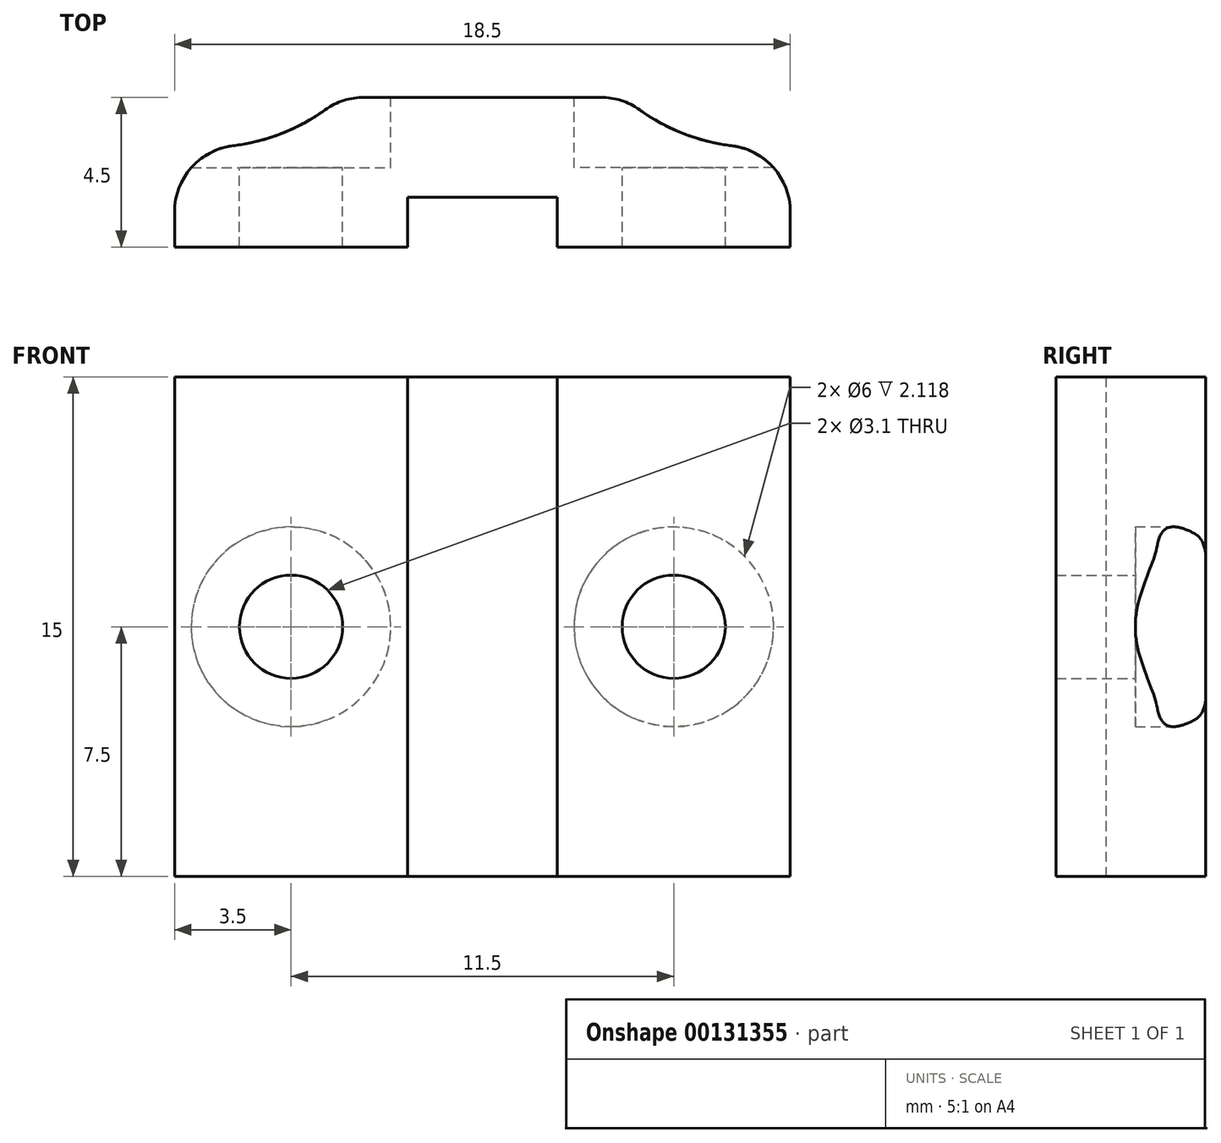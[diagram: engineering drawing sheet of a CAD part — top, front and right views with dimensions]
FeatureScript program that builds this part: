
annotation { "Feature Type Name" : "Feature", "Feature Type Description" : "" }
export const myFeature = defineFeature(function(context is Context, id is Id, definition is map)
    precondition{}
    {
        {
            var Q0;
            Q0=qCreatedBy(makeId("Top.planeOp"),FACE);
            var sketch = newSketch(context, id + "F0", { "sketchPlane" : qUnion([Q0])});
            skLineSegment(sketch, "E0", {"start": v(0, 0) * mm, "end": v(0, 3) * mm});
            skLineSegment(sketch, "E1", {"start": v(0, 3) * mm, "end": v(5, 3) * mm});
            skLineSegment(sketch, "E2", {"start": v(5, 3) * mm, "end": v(5, 4.5) * mm});
            skLineSegment(sketch, "E3", {"start": v(5, 4.5) * mm, "end": v(13.5, 4.5) * mm});
            skLineSegment(sketch, "E4", {"start": v(13.5, 4.5) * mm, "end": v(13.5, 3) * mm});
            skLineSegment(sketch, "E5", {"start": v(13.5, 3) * mm, "end": v(18.5, 3) * mm});
            skLineSegment(sketch, "E6", {"start": v(18.5, 3) * mm, "end": v(18.5, 0) * mm});
            skLineSegment(sketch, "E7", {"start": v(18.5, 0) * mm, "end": v(11.5, 0) * mm});
            skLineSegment(sketch, "E8", {"start": v(11.5, 0) * mm, "end": v(11.5, 1.5) * mm});
            skLineSegment(sketch, "E9", {"start": v(11.5, 1.5) * mm, "end": v(7, 1.5) * mm});
            skLineSegment(sketch, "E10", {"start": v(7, 1.5) * mm, "end": v(7, 0) * mm});
            skLineSegment(sketch, "E11", {"start": v(7, 0) * mm, "end": v(0, 0) * mm});
            skSolve(sketch);
        }
        {
            var Q0;
            Q0=qSketchRegion(id+"F0",true);
            extrude(context, id + "F1", {"entities" : qUnion([Q0]), "depth" : 15 * mm});
        }
        {
            var Q0;
            Q0=makeQuery(id+"F1.opExtrude","SWEPT_FACE",FACE,{"disambiguationData":[OSD([sQuery(id+"F0.wireOp",EDGE,"E3")])]});
            cPlane(context, id + "F2", {"entities" : qUnion([Q0]), "cplaneType" : CPlaneType.OFFSET, "offset" : 0 * mm, "width" : 150 * mm, "height" : 150 * mm});
        }
        {
            var Q0;
            Q0=makeQuery(id+"F1.opExtrude","SWEPT_EDGE",EDGE,{"disambiguationData":[OSD([sQuery(id+"F0.wireOp",EDGE,"E4"),sQuery(id+"F0.wireOp",EDGE,"E5")])]});
            var Q1;
            Q1=makeQuery(id+"F1.opExtrude","SWEPT_EDGE",EDGE,{"disambiguationData":[OSD([sQuery(id+"F0.wireOp",EDGE,"E1"),sQuery(id+"F0.wireOp",EDGE,"E2")])]});
            fillet(context, id + "F3", {"entities" : qUnion([Q0, Q1]), "radius" : 6 * mm, "tangentPropagation" : true, "allowEdgeOverflow" : false});
        }
        {
            var Q0;
            Q0=makeQuery(id+"F3.opFillet","BLEND_EDGE",EDGE,{"blendedFrom":[makeQuery(id+"F1.opExtrude","SWEPT_EDGE",EDGE,{"disambiguationData":[OSD([sQuery(id+"F0.wireOp",EDGE,"E4"),sQuery(id+"F0.wireOp",EDGE,"E5")])]}),makeQuery(id+"F1.opExtrude","SWEPT_FACE",FACE,{"disambiguationData":[OSD([sQuery(id+"F0.wireOp",EDGE,"E3")])]})],"blendedInto":[makeQuery(id+"F1.opExtrude","SWEPT_FACE",FACE,{"disambiguationData":[OSD([sQuery(id+"F0.wireOp",EDGE,"E3")])]})]});
            var Q1;
            Q1=makeQuery(id+"F3.opFillet","BLEND_EDGE",EDGE,{"blendedFrom":[makeQuery(id+"F1.opExtrude","SWEPT_EDGE",EDGE,{"disambiguationData":[OSD([sQuery(id+"F0.wireOp",EDGE,"E1"),sQuery(id+"F0.wireOp",EDGE,"E2")])]}),makeQuery(id+"F1.opExtrude","SWEPT_FACE",FACE,{"disambiguationData":[OSD([sQuery(id+"F0.wireOp",EDGE,"E3")])]})],"blendedInto":[makeQuery(id+"F1.opExtrude","SWEPT_FACE",FACE,{"disambiguationData":[OSD([sQuery(id+"F0.wireOp",EDGE,"E3")])]})]});
            var Q2;
            Q2=makeQuery(id+"F1.opExtrude","SWEPT_EDGE",EDGE,{"disambiguationData":[OSD([sQuery(id+"F0.wireOp",EDGE,"E5"),sQuery(id+"F0.wireOp",EDGE,"E6")])]});
            var Q3;
            Q3=makeQuery(id+"F1.opExtrude","SWEPT_EDGE",EDGE,{"disambiguationData":[OSD([sQuery(id+"F0.wireOp",EDGE,"E0"),sQuery(id+"F0.wireOp",EDGE,"E1")])]});
            fillet(context, id + "F4", {"entities" : qUnion([Q0, Q1, Q2, Q3]), "radius" : 2 * mm, "tangentPropagation" : true, "allowEdgeOverflow" : false});
        }
        {
            var Q0;
            Q0=qCreatedBy(id+"F2.planeOp",FACE);
            var sketch = newSketch(context, id + "F5", { "sketchPlane" : qUnion([Q0])});
            skPoint(sketch, "E12", {"position": v(-15, 7.5) * mm});
            skPoint(sketch, "E13", {"position": v(-3.5, 7.5) * mm});
            skSolve(sketch);
        }
        {
            var Q0;
            Q0=sQuery(id+"F5.wireOp",VERTEX,"E12");
            var Q1;
            Q1=sQuery(id+"F5.wireOp",VERTEX,"E13");
            var Q2;
            Q2=makeQuery(id+"F1.opExtrude","SWEPT_BODY",BODY,{"disambiguationData":[OSD([sQuery(id+"F0.wireOp",EDGE,"E0"),sQuery(id+"F0.wireOp",EDGE,"E1"),sQuery(id+"F0.wireOp",EDGE,"E2"),sQuery(id+"F0.wireOp",EDGE,"E3"),sQuery(id+"F0.wireOp",EDGE,"E4"),sQuery(id+"F0.wireOp",EDGE,"E5"),sQuery(id+"F0.wireOp",EDGE,"E6"),sQuery(id+"F0.wireOp",EDGE,"E7"),sQuery(id+"F0.wireOp",EDGE,"E8"),sQuery(id+"F0.wireOp",EDGE,"E9"),sQuery(id+"F0.wireOp",EDGE,"E10"),sQuery(id+"F0.wireOp",EDGE,"E11")])]});
            hole(context, id + "F6", {"style" : HoleStyle.C_BORE, "endStyle" : HoleEndStyle.BLIND, "holeDiameter" : 3.1 * mm, "cBoreDiameter" : 6 * mm, "cBoreDepth" : 0 * mm, "holeDepth" : 12 * mm, "locations" : qUnion([Q0, Q1]), "scope" : qUnion([Q2])});
        }
    });
